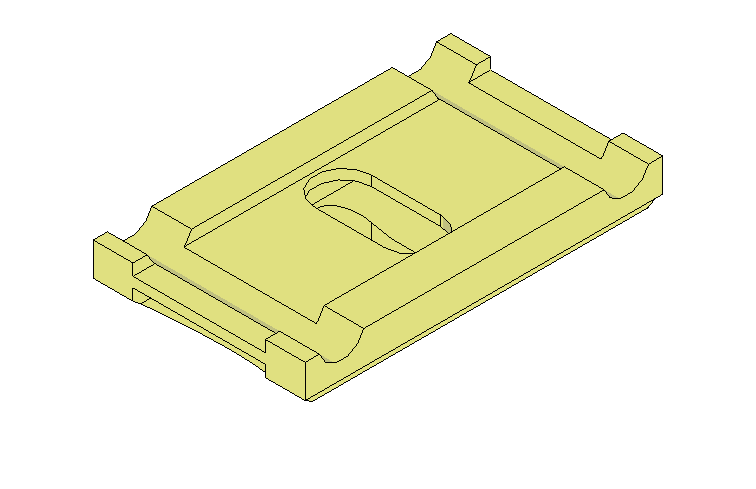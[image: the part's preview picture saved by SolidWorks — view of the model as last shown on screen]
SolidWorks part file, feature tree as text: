
SOLIDWORKS PART (.sldprt)
format: sldprt  version: not decoded by parser v0  size: 461,824 bytes
history: native  units: mm
features: sketch x5, plane x3, cut_extrude x3, extrude x2, material x1, pattern_circular x1 (+10 scaffold rows collapsed)
feature tree (25):
  scaffold x10  (default folders/planes/origin — collapsed)
  material  "Matériau <non spécifié>"
  plane  "Plan de face"
  plane  "Plan de dessus"
  plane  "Plan de droite"
  sketch  "Esquisse1"  dims[c1.D6=~18.923635mm c1.D4=22.5mm c1.D1=32.0mm c1.D2=1.5mm c1.D3=5.0mm c2.D4=12.0mm c2.D5=20.0mm c2.D6=3.0mm]
  extrude  "Extrusion1"  Depth=54mm
  sketch  "Esquisse2"  dims[D1=19.0mm D2=8.5mm]
  cut_extrude  "Enlèv. mat.-Extru.1"  [1 undecoded]
  sketch  "Esquisse3"  dims[c1.D1=7.0mm c1.D3=7.0mm c1.D2=1.0mm c2.D3=43.0mm]
  cut_extrude  "Enlèv. mat.-Extru.2"  [1 undecoded]
  sketch  "Esquisse5"  dims[D1=37.0mm]
  cut_extrude  "Enlèv. mat.-Extru.3"  [1 undecoded]
  sketch  "Esquisse6"  dims[c1.D1=1.2mm c1.D2=23.0mm c1.D3=~15.661163mm c2.D3=42.0deg c2.D4=1.2mm c2.D5=23.0mm]
  extrude  "Extrusion2"  [1 undecoded]
  pattern_circular  "Répétition circulaire1"  Count=22 Angle=4deg
decode coverage: 7 of 11 modeling features carry decoded parameters
note: ~ marks probable driven/reference dimensions
note: 4 parameter values undecoded
summary: no parameter record found for 4 features
note: suppression state not decoded; provenance and decode notes live in map.json
